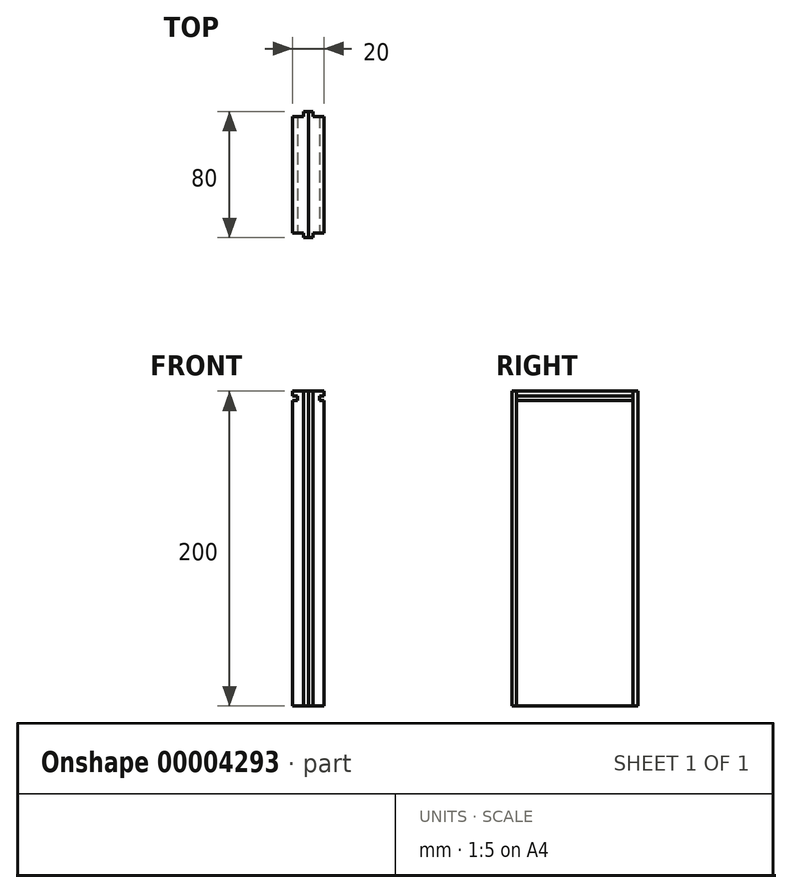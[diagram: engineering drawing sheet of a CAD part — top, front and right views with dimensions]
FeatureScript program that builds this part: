
annotation { "Feature Type Name" : "Feature", "Feature Type Description" : "" }
export const myFeature = defineFeature(function(context is Context, id is Id, definition is map)
    precondition{}
    {
        {
            var Q0;
            Q0=qCreatedBy(makeId("Right.planeOp"),FACE);
            var sketch = newSketch(context, id + "F0", { "sketchPlane" : qUnion([Q0])});
            skLineSegment(sketch, "E0", {"start": v(76.05, 185.6) * mm, "end": v(2.05, 185.6) * mm});
            skLineSegment(sketch, "E1", {"start": v(2.05, 185.6) * mm, "end": v(2.05, -14.4) * mm});
            skLineSegment(sketch, "E2", {"start": v(2.05, -14.4) * mm, "end": v(76.05, -14.4) * mm});
            skLineSegment(sketch, "E3", {"start": v(76.05, -14.4) * mm, "end": v(76.05, 185.6) * mm});
            skSolve(sketch);
        }
        {
            var Q0;
            Q0=makeQuery(id+"F0.imprint","IMPRINT",FACE,{"disambiguationData":[TD([[makeQuery(id+"F0.imprint","IMPRINT",EDGE,{"derivedFrom":sQuery(id+"F0.wireOp",EDGE,"E0")}),1.0]])]});
            extrude(context, id + "F1", {"entities" : qUnion([Q0]), "depth" : 10 * mm});
        }
        {
            var Q0;
            Q0=makeQuery(id+"F1.opExtrude","SWEPT_FACE",FACE,{"disambiguationData":[OSD([sQuery(id+"F0.wireOp",EDGE,"E1")])]});
            var sketch = newSketch(context, id + "F2", { "sketchPlane" : qUnion([Q0])});
            skLineSegment(sketch, "E4.0", {"start": v(3, 185.6) * mm, "end": v(3, -14.4) * mm});
            skSolve(sketch);
        }
        {
            var Q0;
            {var subQ2=sQuery(id+"F2.wireOp",EDGE,"E4.0");Q0=makeQuery(id+"F2.imprint","IMPRINT",FACE,{"disambiguationData":[TD([[makeQuery(id+"F2.imprint","IMPRINT",EDGE,{"derivedFrom":subQ2}),-1.0]])]});}
            extrude(context, id + "F3", {"entities" : qUnion([Q0]), "operationType" : NewBodyOperationType.ADD, "depth" : 3 * mm});
        }
        {
            var Q0;
            Q0=makeQuery(id+"F1.opExtrude","SWEPT_FACE",FACE,{"disambiguationData":[OSD([sQuery(id+"F0.wireOp",EDGE,"E3")])]});
            var sketch = newSketch(context, id + "F4", { "sketchPlane" : qUnion([Q0])});
            skLineSegment(sketch, "E5.0", {"start": v(-3, -14.4) * mm, "end": v(-3, 185.6) * mm});
            skSolve(sketch);
        }
        {
            var Q0;
            {var subQ2=sQuery(id+"F4.wireOp",EDGE,"E5.0");Q0=makeQuery(id+"F4.imprint","IMPRINT",FACE,{"disambiguationData":[TD([[makeQuery(id+"F4.imprint","IMPRINT",EDGE,{"derivedFrom":subQ2}),-1.0]])]});}
            extrude(context, id + "F5", {"entities" : qUnion([Q0]), "operationType" : NewBodyOperationType.ADD, "depth" : 3 * mm});
        }
        {
            var Q0;
            Q0=makeQuery(id+"F1.opExtrude","CAP_FACE",FACE,{"disambiguationData":[OSD([sQuery(id+"F0.wireOp",EDGE,"E0"),sQuery(id+"F0.wireOp",EDGE,"E1"),sQuery(id+"F0.wireOp",EDGE,"E2"),sQuery(id+"F0.wireOp",EDGE,"E3")])],"isStart":false});
            var sketch = newSketch(context, id + "F6", { "sketchPlane" : qUnion([Q0])});
            skLineSegment(sketch, "E6.0", {"start": v(76.05, 182.6) * mm, "end": v(2.05, 182.6) * mm});
            skLineSegment(sketch, "E7.0", {"start": v(76.05, 179.6) * mm, "end": v(2.05, 179.6) * mm});
            skSolve(sketch);
        }
        {
            var Q0;
            {var subQ2=sQuery(id+"F6.wireOp",EDGE,"E6.0");Q0=makeQuery(id+"F6.imprint","IMPRINT",FACE,{"disambiguationData":[TD([[makeQuery(id+"F6.imprint","IMPRINT",EDGE,{"derivedFrom":subQ2}),1.0]])]});}
            extrude(context, id + "F7", {"entities" : qUnion([Q0]), "operationType" : NewBodyOperationType.REMOVE, "oppositeDirection" : true, "depth" : 3 * mm});
        }
        {
            var Q0;
            Q0=makeQuery(id+"F1.opExtrude","SWEPT_BODY",BODY,{"disambiguationData":[OSD([sQuery(id+"F0.wireOp",EDGE,"E0"),sQuery(id+"F0.wireOp",EDGE,"E1"),sQuery(id+"F0.wireOp",EDGE,"E2"),sQuery(id+"F0.wireOp",EDGE,"E3")])]});
            var Q1;
            Q1=qCreatedBy(makeId("Right.planeOp"),FACE);
            mirror(context, id + "F8", {"entities" : qUnion([Q0]), "mirrorPlane" : qUnion([Q1])});
        }
    });
